# Revit family: TRA30-PM
name_source: partatom
category: Lighting Fixtures
units: mm (PartAtom-declared; Revit-internal decimal feet)

## family parameters
Cut with Voids When Loaded = No
Host = Face
Light Source = Yes
OmniClass Number = 23.80.70.11
OmniClass Title = Luminaries for Internal Lighting
Part Type = Normal
Room Calculation Point = No
Round Connector Dimension = Use Diameter
Shared = No

## types (1)
- TRA30
    Apparent Load = 0 VA
    Color Filter = 16777215
    Default Elevation = 48.000"
    Description = 30 Inch Traditional Luminaire
    Dimming Lamp Color Temperature Shift = <None>
    Emit Shape Visible in Rendering = No
    Emit from Rectangle Length = 4.000"
    Emit from Rectangle Width = 4.000"
    Finish = Paint - Basic Black Textured
    Lamp = LED Array
    Light Bulb Material = Glass
    Manufacturer = Beacon Products
    Model = Traditional-PM
    Photometric Web File = TRA30-AC-60NB-136-5K-UNV-DIR5.ies
    Tilt Angle = 90.00°
    URL = https://www.currentlighting.com
    Voltage = 120 V
    Wattage Comments = 55-136 W

## geometry (parser evidence)
native form markers: Blend x1, Sweep x6
no freeform markers — native parametric forms only
